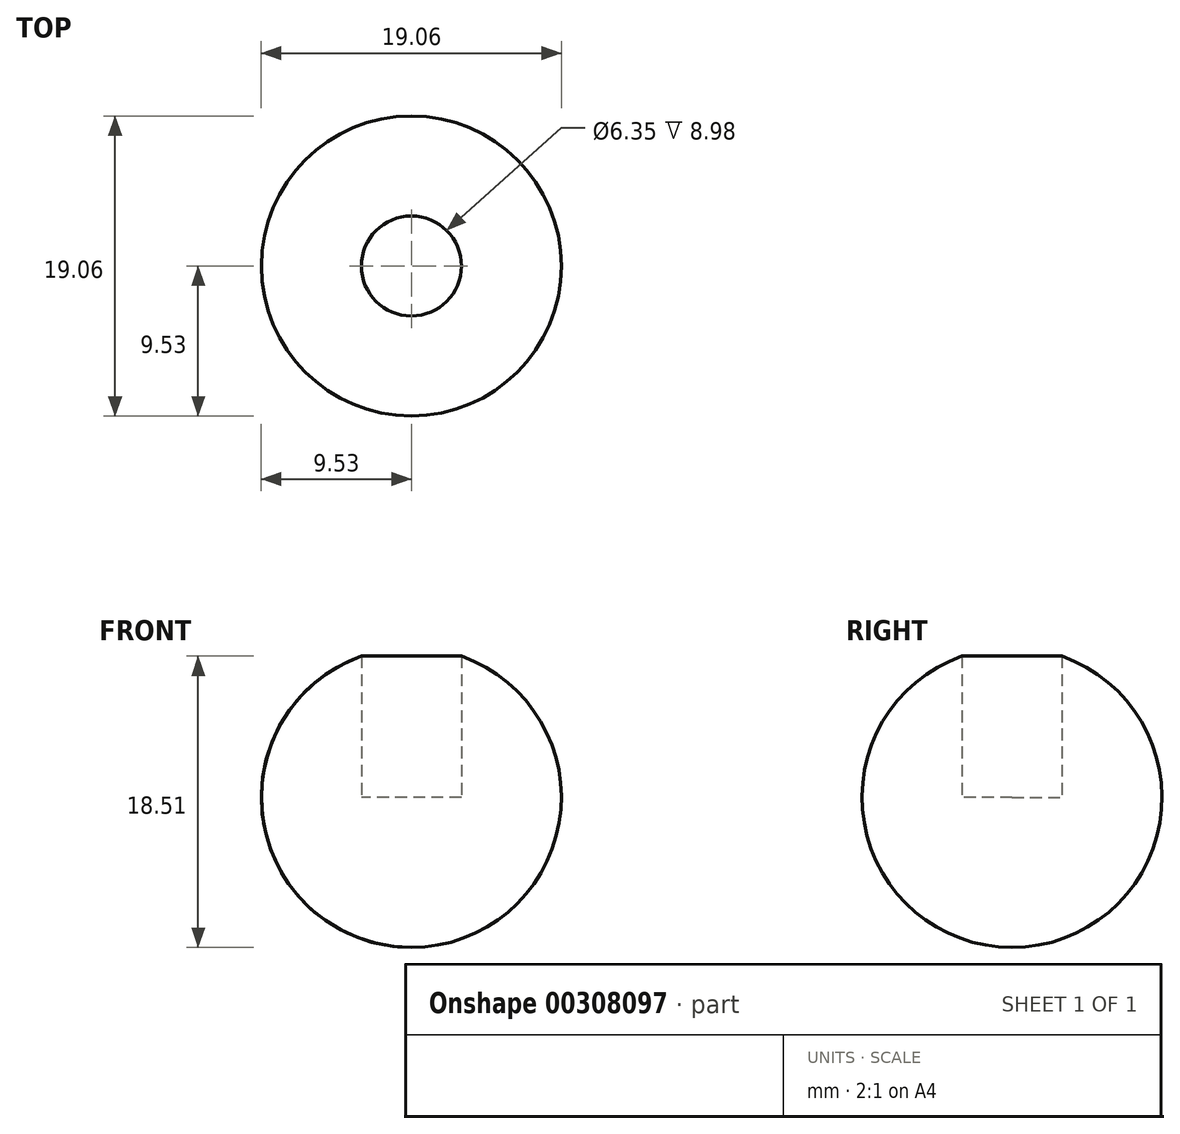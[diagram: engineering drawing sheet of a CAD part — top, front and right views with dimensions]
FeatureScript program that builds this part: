
annotation { "Feature Type Name" : "Feature", "Feature Type Description" : "" }
export const myFeature = defineFeature(function(context is Context, id is Id, definition is map)
    precondition{}
    {
        {
            var Q0;
            Q0=qCreatedBy(makeId("Front.planeOp"),FACE);
            var sketch = newSketch(context, id + "F0", { "sketchPlane" : qUnion([Q0])});
            skArc(sketch, "E0", {"start": v(0, 9.52) * mm, "mid": v(-9.52, 0) * mm, "end": v(0, -9.52) * mm});
            skLineSegment(sketch, "E1", {"start": v(0, 9.52) * mm, "end": v(0, -9.52) * mm});
            skSolve(sketch);
        }
        {
            var Q0;
            Q0=qCreatedBy(makeId("Top.planeOp"),FACE);
            var sketch = newSketch(context, id + "F1", { "sketchPlane" : qUnion([Q0])});
            skCircle(sketch, "E2", {"center": v(0, 0) * mm, "radius": 9.53 * mm});
            skSolve(sketch);
        }
        {
            var Q0;
            Q0=makeQuery(id+"F0.imprint","IMPRINT",FACE,{"disambiguationData":[TD([[makeQuery(id+"F0.imprint","IMPRINT",EDGE,{"derivedFrom":sQuery(id+"F0.wireOp",EDGE,"E0")}),1.0]])]});
            var Q1;
            Q1=sQuery(id+"F1.wireOp",EDGE,"E2");
            revolve(context, id + "F2", {"entities" : qUnion([Q0]), "axis" : qUnion([Q1]), "revolveType" : RevolveType.FULL});
        }
        {
            var Q0;
            Q0=qCreatedBy(makeId("Top.planeOp"),FACE);
            var sketch = newSketch(context, id + "F3", { "sketchPlane" : qUnion([Q0])});
            skCircle(sketch, "E3", {"center": v(0, 0) * mm, "radius": 3.18 * mm});
            skSolve(sketch);
        }
        {
            var Q0;
            Q0 = qSketchRegion(id + "F3", true);
            extrude(context, id + "F4", {"entities" : qUnion([Q0]), "operationType" : NewBodyOperationType.REMOVE, "depth" : 25.4 * mm});
        }
    });
